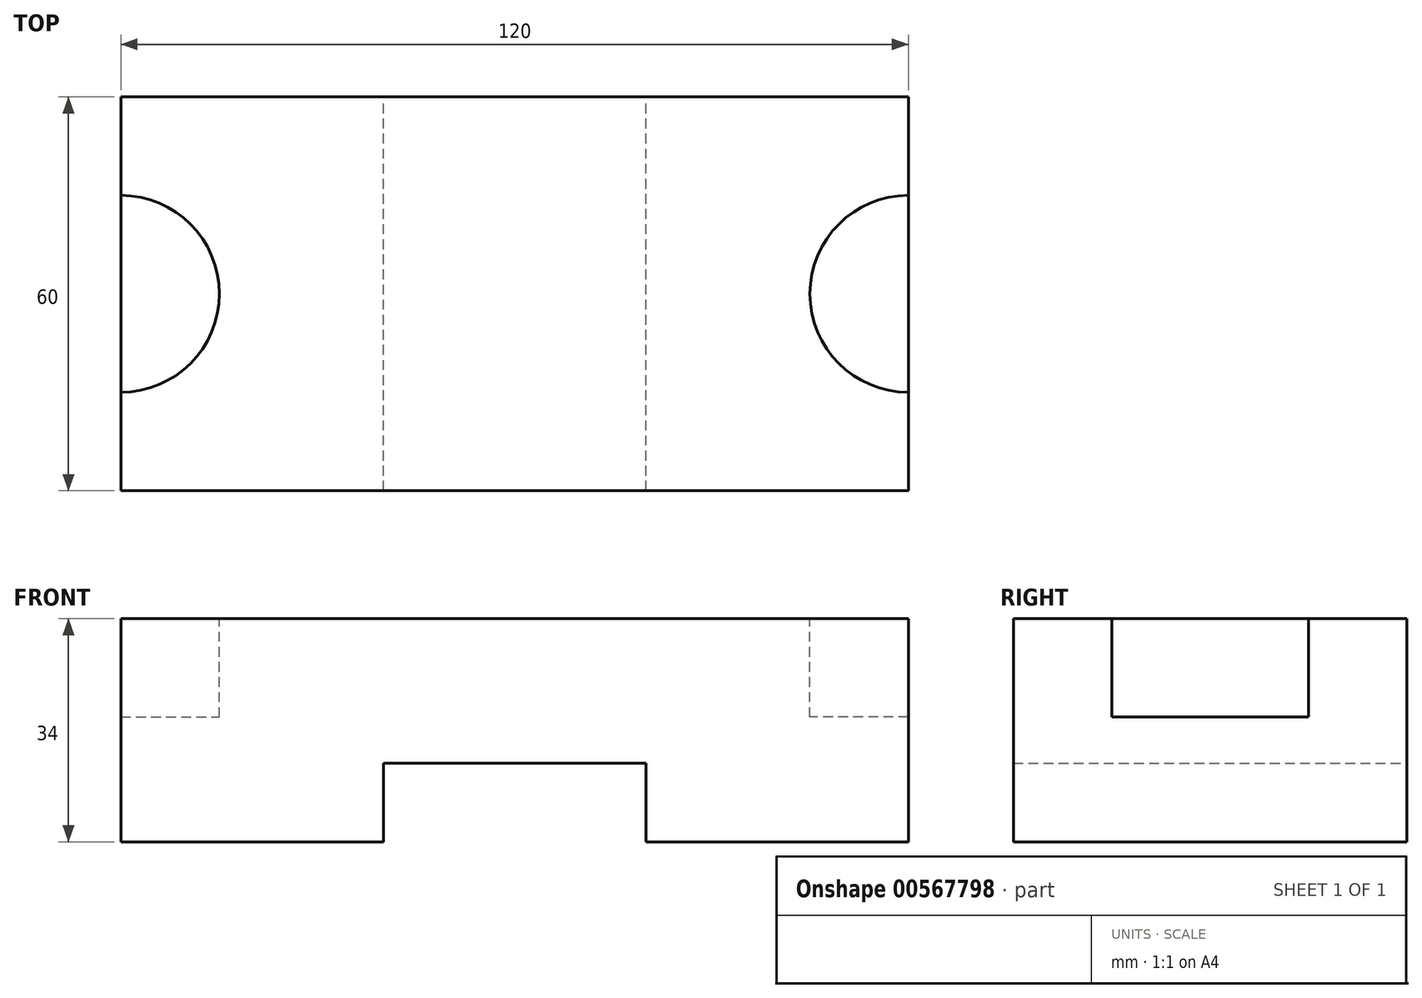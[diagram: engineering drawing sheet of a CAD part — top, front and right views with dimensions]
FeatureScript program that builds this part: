
annotation { "Feature Type Name" : "Feature", "Feature Type Description" : "" }
export const myFeature = defineFeature(function(context is Context, id is Id, definition is map)
    precondition{}
    {
        {
            var Q0;
            Q0=qCreatedBy(makeId("Front.planeOp"),FACE);
            var sketch = newSketch(context, id + "F0", { "sketchPlane" : qUnion([Q0])});
            skLineSegment(sketch, "E0.bottom", {"start": v(-60, 17) * mm, "end": v(60, 17) * mm});
            skLineSegment(sketch, "E0.top", {"start": v(-60, -17) * mm, "end": v(-20, -17) * mm});
            skLineSegment(sketch, "E0.left", {"start": v(-60, 17) * mm, "end": v(-60, -17) * mm});
            skLineSegment(sketch, "E0.right", {"start": v(60, 17) * mm, "end": v(60, -17) * mm});
            skPoint(sketch, "E0.middle", {"position": v(0, 0) * mm});
            skLineSegment(sketch, "E1.bottom", {"start": v(-20, -5) * mm, "end": v(20, -5) * mm});
            skLineSegment(sketch, "E1.left", {"start": v(-20, -5) * mm, "end": v(-20, -17) * mm});
            skLineSegment(sketch, "E1.right", {"start": v(20, -5) * mm, "end": v(20, -17) * mm});
            skPoint(sketch, "E1.middle", {"position": v(0, -17) * mm});
            skPoint(sketch, "E2.orphan", {"position": v(-20, -29) * mm});
            skPoint(sketch, "E3.orphan", {"position": v(20, -29) * mm});
            skLineSegment(sketch, "E4.trimOffspring", {"start": v(20, -17) * mm, "end": v(60, -17) * mm});
            skSolve(sketch);
        }
        {
            var Q0;
            Q0=makeQuery(id+"F0.imprint","IMPRINT",FACE,{"disambiguationData":[TD([[makeQuery(id+"F0.imprint","IMPRINT",EDGE,{"derivedFrom":sQuery(id+"F0.wireOp",EDGE,"E0.bottom")}),-1.0]])]});
            extrude(context, id + "F1", {"entities" : qUnion([Q0]), "depth" : 60 * mm, "offsetDistance" : 25 * mm});
        }
        {
            var Q0;
            Q0=makeQuery(id+"F1.opExtrude","SWEPT_FACE",FACE,{"disambiguationData":[OSD([sQuery(id+"F0.wireOp",EDGE,"E0.bottom")])]});
            var sketch = newSketch(context, id + "F2", { "sketchPlane" : qUnion([Q0])});
            skArc(sketch, "E5", {"start": v(60, -15) * mm, "mid": v(45, -30) * mm, "end": v(60, -45) * mm});
            skArc(sketch, "E6", {"start": v(-60, -45) * mm, "mid": v(-45, -30) * mm, "end": v(-60, -15) * mm});
            skLineSegment(sketch, "E7", {"start": v(60, -7.95) * mm, "end": v(60, -52.87) * mm});
            skLineSegment(sketch, "E8", {"start": v(-60, -8.22) * mm, "end": v(-60, -52.87) * mm});
            skSolve(sketch);
        }
        {
            var Q0;
            {var subQ0=sQuery(id+"F2.wireOp",EDGE,"E6");Q0=makeQuery(id+"F2.imprint","IMPRINT",FACE,{"disambiguationData":[TD([[makeQuery(id+"F2.imprint","IMPRINT",EDGE,{"derivedFrom":subQ0}),1.0]])]});}
            var Q1;
            {var subQ0=sQuery(id+"F2.wireOp",EDGE,"E5");Q1=makeQuery(id+"F2.imprint","IMPRINT",FACE,{"disambiguationData":[TD([[makeQuery(id+"F2.imprint","IMPRINT",EDGE,{"derivedFrom":subQ0}),1.0]])]});}
            extrude(context, id + "F3", {"entities" : qUnion([Q0, Q1]), "operationType" : NewBodyOperationType.REMOVE, "oppositeDirection" : true, "depth" : 15 * mm, "offsetDistance" : 25 * mm});
        }
    });
